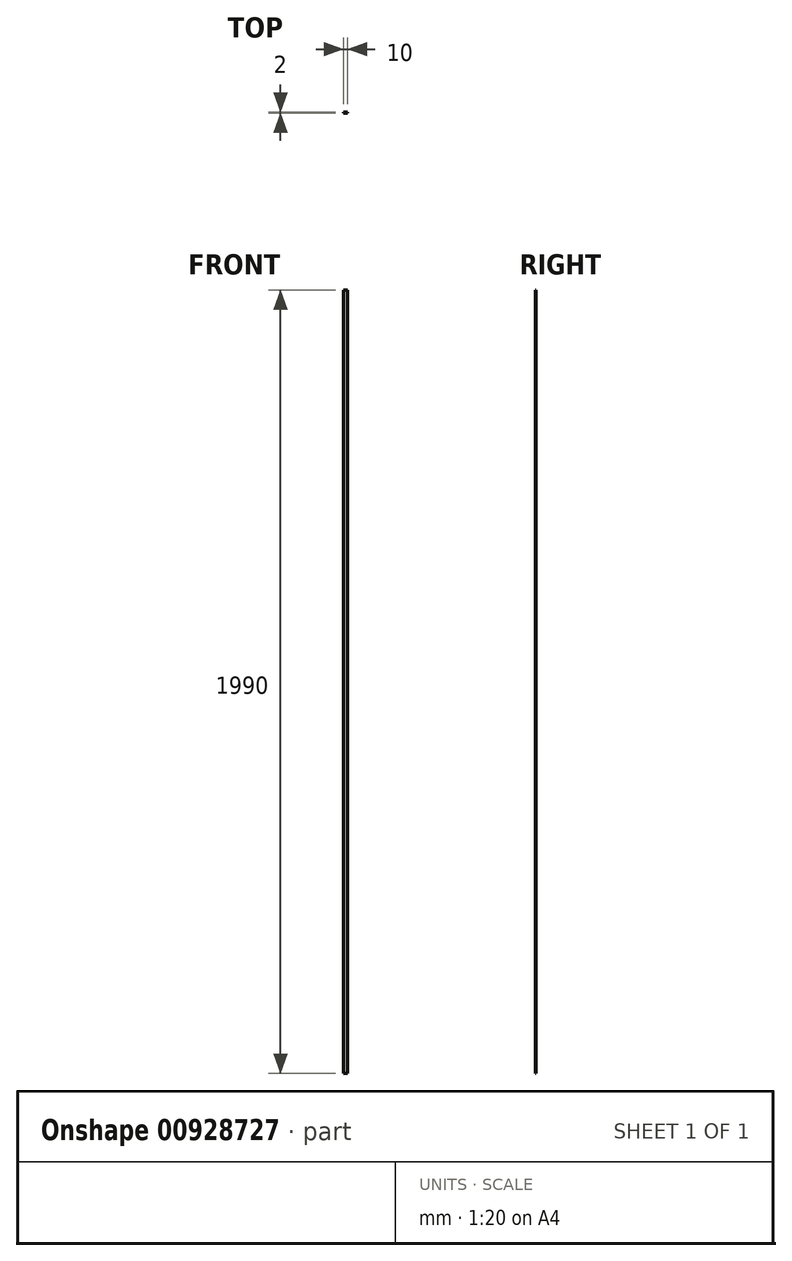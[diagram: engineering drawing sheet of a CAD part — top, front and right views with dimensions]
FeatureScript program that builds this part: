
annotation { "Feature Type Name" : "Feature", "Feature Type Description" : "" }
export const myFeature = defineFeature(function(context is Context, id is Id, definition is map)
    precondition{}
    {
        {
            var Q0;
            Q0=qCreatedBy(makeId("Front.planeOp"),FACE);
            var sketch = newSketch(context, id + "F0", { "sketchPlane" : qUnion([Q0])});
            skLineSegment(sketch, "E0.bottom", {"start": v(0, 0) * mm, "end": v(10, 0) * mm});
            skLineSegment(sketch, "E0.top", {"start": v(0, 1990) * mm, "end": v(10, 1990) * mm});
            skLineSegment(sketch, "E0.left", {"start": v(0, 0) * mm, "end": v(0, 1990) * mm});
            skLineSegment(sketch, "E0.right", {"start": v(10, 0) * mm, "end": v(10, 1990) * mm});
            skSolve(sketch);
        }
        {
            var Q0;
            Q0=makeQuery(id+"F0.imprint","IMPRINT",FACE,{"disambiguationData":[TD([[makeQuery(id+"F0.imprint","IMPRINT",EDGE,{"derivedFrom":sQuery(id+"F0.wireOp",EDGE,"E0.bottom")}),1.0]])]});
            extrude(context, id + "F1", {"entities" : qUnion([Q0]), "depth" : 2 * mm, "offsetDistance" : 25 * mm});
        }
    });
